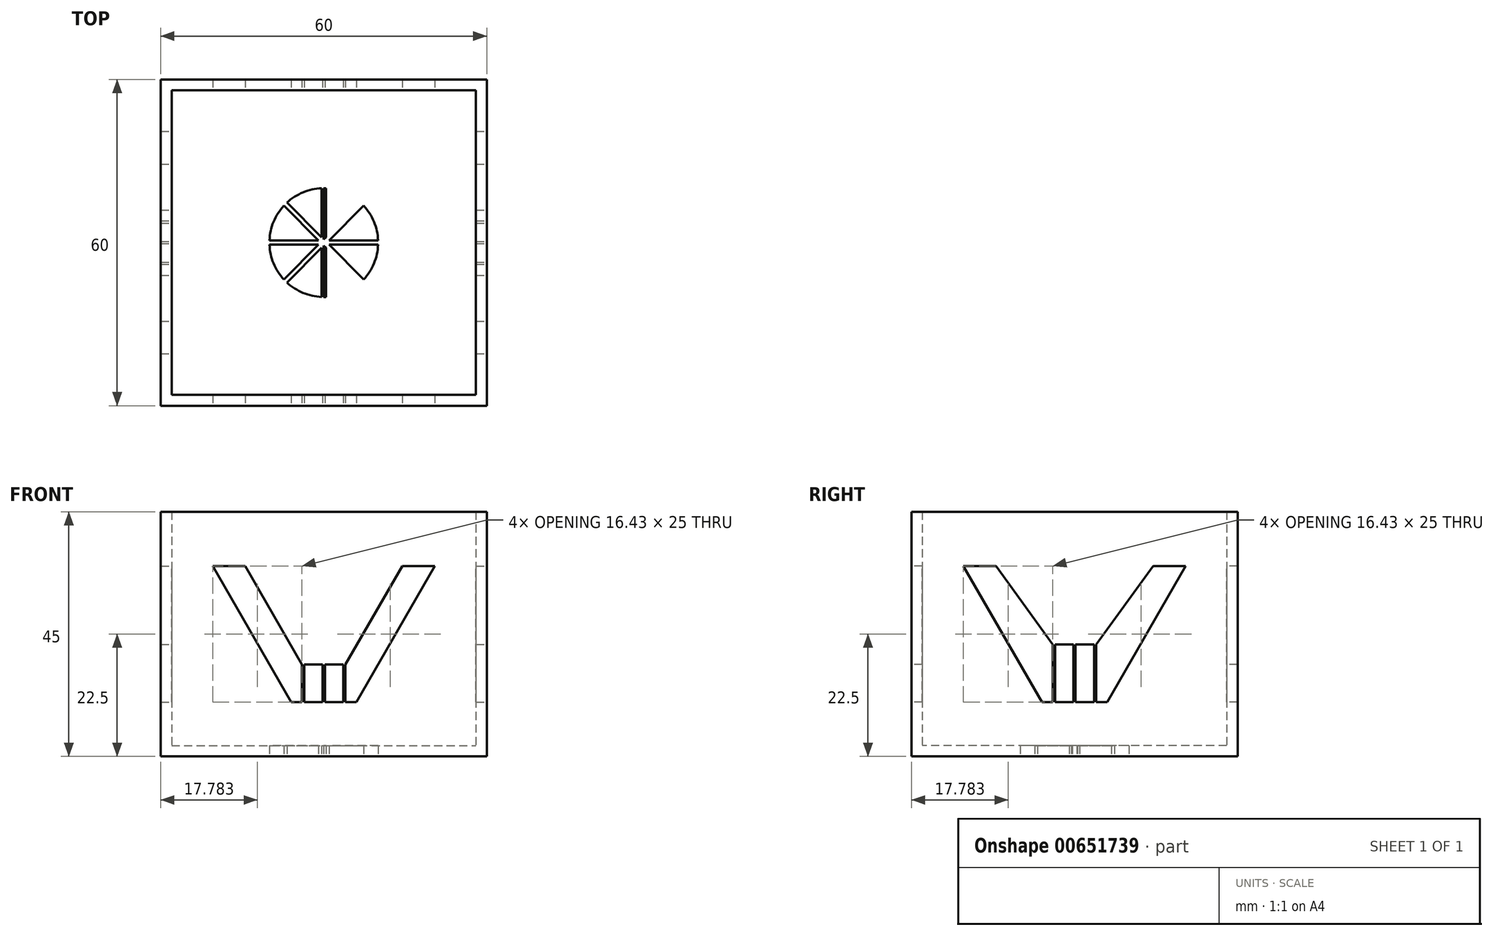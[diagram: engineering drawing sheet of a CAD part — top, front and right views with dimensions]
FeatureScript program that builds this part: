
annotation { "Feature Type Name" : "Feature", "Feature Type Description" : "" }
export const myFeature = defineFeature(function(context is Context, id is Id, definition is map)
    precondition{}
    {
        {
            var Q0;
            Q0=qCreatedBy(makeId("Top.planeOp"),FACE);
            var sketch = newSketch(context, id + "F0", { "sketchPlane" : qUnion([Q0])});
            skLineSegment(sketch, "E0.bottom", {"start": v(-30, 30) * mm, "end": v(30, 30) * mm});
            skLineSegment(sketch, "E0.top", {"start": v(-30, -30) * mm, "end": v(30, -30) * mm});
            skLineSegment(sketch, "E0.left", {"start": v(-30, 30) * mm, "end": v(-30, -30) * mm});
            skLineSegment(sketch, "E0.right", {"start": v(30, 30) * mm, "end": v(30, -30) * mm});
            skSolve(sketch);
        }
        {
            var Q0;
            Q0=makeQuery(id+"F0.imprint","IMPRINT",FACE,{"disambiguationData":[TD([[makeQuery(id+"F0.imprint","IMPRINT",EDGE,{"derivedFrom":sQuery(id+"F0.wireOp",EDGE,"E0.bottom")}),-1.0]])]});
            var Q1;
            Q1 = qSketchRegion(id + "F3", true);
            extrude(context, id + "F1", {"entities" : qUnion([Q0, Q1]), "depth" : 45 * mm, "offsetDistance" : 25 * mm});
        }
        {
            var Q0;
            Q0=makeQuery(id+"F1.opExtrude","CAP_FACE",FACE,{"disambiguationData":[OSD([sQuery(id+"F0.wireOp",EDGE,"E0.bottom"),sQuery(id+"F0.wireOp",EDGE,"E0.top"),sQuery(id+"F0.wireOp",EDGE,"E0.left"),sQuery(id+"F0.wireOp",EDGE,"E0.right")])],"isStart":false});
            shell(context, id + "F2", {"entities" : qUnion([Q0]), "thickness" : 2 * mm});
        }
        {
            var Q0;
            Q0=makeQuery(id+"F1.opExtrude","SWEPT_FACE",FACE,{"disambiguationData":[OSD([sQuery(id+"F0.wireOp",EDGE,"E0.top")])]});
            var sketch = newSketch(context, id + "F3", { "sketchPlane" : qUnion([Q0])});
            skLineSegment(sketch, "E1", {"start": v(-6, 10) * mm, "end": v(6, 10) * mm});
            skLineSegment(sketch, "E2", {"start": v(6, 10) * mm, "end": v(20.43, 35) * mm});
            skLineSegment(sketch, "E3", {"start": v(-6, 10) * mm, "end": v(-20.43, 35) * mm});
            skLineSegment(sketch, "E4", {"start": v(20.43, 35) * mm, "end": v(20.43, 45) * mm});
            skLineSegment(sketch, "E5", {"start": v(-20.43, 35) * mm, "end": v(-14.43, 35) * mm});
            skLineSegment(sketch, "E6", {"start": v(20.43, 35) * mm, "end": v(14.43, 35) * mm});
            skLineSegment(sketch, "E7", {"start": v(-14.43, 35) * mm, "end": v(-4, 16.93) * mm});
            skLineSegment(sketch, "E8", {"start": v(14.43, 35) * mm, "end": v(4, 16.93) * mm});
            skLineSegment(sketch, "E9", {"start": v(-4, 16.93) * mm, "end": v(4, 16.93) * mm});
            skLineSegment(sketch, "E10", {"start": v(-4, 16.93) * mm, "end": v(-4, 10) * mm});
            skLineSegment(sketch, "E11", {"start": v(-3.6, 16.93) * mm, "end": v(-3.6, 10) * mm});
            skLineSegment(sketch, "E12", {"start": v(4, 16.93) * mm, "end": v(4, 10) * mm});
            skLineSegment(sketch, "E13", {"start": v(3.6, 16.93) * mm, "end": v(3.6, 10) * mm});
            skLineSegment(sketch, "E14", {"start": v(0, 16.93) * mm, "end": v(0, 10) * mm});
            skLineSegment(sketch, "E15", {"start": v(0.2, 16.93) * mm, "end": v(0.2, 10) * mm});
            skLineSegment(sketch, "E16", {"start": v(-0.2, 16.93) * mm, "end": v(-0.2, 10) * mm});
            skSolve(sketch);
        }
        {
            var Q0;
            {var subQ0=sQuery(id+"F3.wireOp",EDGE,"E3");Q0=makeQuery(id+"F3.imprint","IMPRINT",FACE,{"disambiguationData":[TD([[makeQuery(id+"F3.imprint","IMPRINT",EDGE,{"derivedFrom":subQ0}),-1.0]])]});}
            var Q1;
            {var subQ0=sQuery(id+"F3.wireOp",EDGE,"E11");Q1=makeQuery(id+"F3.imprint","IMPRINT",FACE,{"disambiguationData":[TD([[makeQuery(id+"F3.imprint","IMPRINT",EDGE,{"derivedFrom":subQ0}),1.0]])]});}
            var Q2;
            {var subQ0=sQuery(id+"F3.wireOp",EDGE,"E13");Q2=makeQuery(id+"F3.imprint","IMPRINT",FACE,{"disambiguationData":[TD([[makeQuery(id+"F3.imprint","IMPRINT",EDGE,{"derivedFrom":subQ0}),-1.0]])]});}
            var Q3;
            {var subQ1=sQuery(id+"F3.wireOp",EDGE,"E2");Q3=makeQuery(id+"F3.imprint","IMPRINT",FACE,{"disambiguationData":[TD([[makeQuery(id+"F3.imprint","IMPRINT",EDGE,{"derivedFrom":subQ1}),1.0]])]});}
            extrude(context, id + "F4", {"entities" : qUnion([Q0, Q1, Q2, Q3]), "operationType" : NewBodyOperationType.REMOVE, "oppositeDirection" : true, "depth" : 64.2 * mm, "offsetDistance" : 25 * mm});
        }
        {
            var Q0;
            Q0=makeQuery(id+"F1.opExtrude","SWEPT_FACE",FACE,{"disambiguationData":[OSD([sQuery(id+"F0.wireOp",EDGE,"E0.right")])]});
            var sketch = newSketch(context, id + "F5", { "sketchPlane" : qUnion([Q0])});
            skLineSegment(sketch, "E17", {"start": v(-6, 10) * mm, "end": v(6, 10) * mm});
            skLineSegment(sketch, "E18", {"start": v(6, 10) * mm, "end": v(20.43, 35) * mm});
            skLineSegment(sketch, "E19", {"start": v(-6, 10) * mm, "end": v(-20.43, 35) * mm});
            skLineSegment(sketch, "E20", {"start": v(-20.43, 35) * mm, "end": v(-14.43, 35) * mm});
            skLineSegment(sketch, "E21", {"start": v(20.43, 35) * mm, "end": v(14.43, 35) * mm});
            skLineSegment(sketch, "E22", {"start": v(-14.43, 35) * mm, "end": v(-4, 20.58) * mm});
            skLineSegment(sketch, "E23", {"start": v(14.43, 35) * mm, "end": v(4, 20.58) * mm});
            skLineSegment(sketch, "E24", {"start": v(-4, 20.58) * mm, "end": v(4, 20.58) * mm});
            skLineSegment(sketch, "E25", {"start": v(-4, 20.58) * mm, "end": v(-4, 10) * mm});
            skLineSegment(sketch, "E26", {"start": v(-3.6, 20.58) * mm, "end": v(-3.6, 10) * mm});
            skLineSegment(sketch, "E27", {"start": v(4, 20.58) * mm, "end": v(4, 10) * mm});
            skLineSegment(sketch, "E28", {"start": v(3.6, 20.58) * mm, "end": v(3.6, 10) * mm});
            skLineSegment(sketch, "E29", {"start": v(0, 20.58) * mm, "end": v(0, 10) * mm});
            skLineSegment(sketch, "E30", {"start": v(0.2, 20.58) * mm, "end": v(0.2, 10) * mm});
            skLineSegment(sketch, "E31", {"start": v(-0.2, 20.58) * mm, "end": v(-0.2, 10) * mm});
            skSolve(sketch);
        }
        {
            var Q0;
            {var subQ0=sQuery(id+"F5.wireOp",EDGE,"E19");Q0=makeQuery(id+"F5.imprint","IMPRINT",FACE,{"disambiguationData":[TD([[makeQuery(id+"F5.imprint","IMPRINT",EDGE,{"derivedFrom":subQ0}),-1.0]])]});}
            var Q1;
            {var subQ0=sQuery(id+"F5.wireOp",EDGE,"E26");Q1=makeQuery(id+"F5.imprint","IMPRINT",FACE,{"disambiguationData":[TD([[makeQuery(id+"F5.imprint","IMPRINT",EDGE,{"derivedFrom":subQ0}),1.0]])]});}
            var Q2;
            {var subQ0=sQuery(id+"F5.wireOp",EDGE,"E28");Q2=makeQuery(id+"F5.imprint","IMPRINT",FACE,{"disambiguationData":[TD([[makeQuery(id+"F5.imprint","IMPRINT",EDGE,{"derivedFrom":subQ0}),-1.0]])]});}
            var Q3;
            {var subQ1=sQuery(id+"F5.wireOp",EDGE,"E18");Q3=makeQuery(id+"F5.imprint","IMPRINT",FACE,{"disambiguationData":[TD([[makeQuery(id+"F5.imprint","IMPRINT",EDGE,{"derivedFrom":subQ1}),1.0]])]});}
            extrude(context, id + "F6", {"entities" : qUnion([Q0, Q1, Q2, Q3]), "operationType" : NewBodyOperationType.REMOVE, "oppositeDirection" : true, "depth" : 63.5 * mm, "offsetDistance" : 25 * mm});
        }
        {
            var Q0;
            Q0=makeQuery(id+"F1.opExtrude","CAP_FACE",FACE,{"disambiguationData":[OSD([sQuery(id+"F0.wireOp",EDGE,"E0.bottom"),sQuery(id+"F0.wireOp",EDGE,"E0.top"),sQuery(id+"F0.wireOp",EDGE,"E0.left"),sQuery(id+"F0.wireOp",EDGE,"E0.right")])],"isStart":true});
            var sketch = newSketch(context, id + "F7", { "sketchPlane" : qUnion([Q0])});
            skCircle(sketch, "E32", {"center": v(0, 0) * mm, "radius": 10 * mm});
            skLineSegment(sketch, "E33", {"start": v(0, 10) * mm, "end": v(0, -10) * mm});
            skLineSegment(sketch, "E34", {"start": v(-10, 0) * mm, "end": v(10, 0) * mm});
            skLineSegment(sketch, "E35", {"start": v(-10, -0.4) * mm, "end": v(10, -0.4) * mm});
            skLineSegment(sketch, "E36", {"start": v(-10, 0.4) * mm, "end": v(10, 0.4) * mm});
            skLineSegment(sketch, "E37", {"start": v(0.4, 10) * mm, "end": v(0.4, -10) * mm});
            skLineSegment(sketch, "E38", {"start": v(-0.4, 10) * mm, "end": v(-0.4, -10) * mm});
            skLineSegment(sketch, "E39", {"start": v(-7.07, -7.07) * mm, "end": v(7.07, 7.07) * mm});
            skLineSegment(sketch, "E40", {"start": v(7.07, -7.07) * mm, "end": v(-7.07, 7.07) * mm});
            skLineSegment(sketch, "E41", {"start": v(-6.78, -7.35) * mm, "end": v(7.35, 6.78) * mm});
            skLineSegment(sketch, "E42", {"start": v(-7.35, -6.78) * mm, "end": v(6.78, 7.35) * mm});
            skLineSegment(sketch, "E43", {"start": v(6.78, -7.35) * mm, "end": v(-7.35, 6.78) * mm});
            skLineSegment(sketch, "E44", {"start": v(7.35, -6.78) * mm, "end": v(-6.78, 7.35) * mm});
            skSolve(sketch);
        }
        {
            var Q0;
            {var subQ0=sQuery(id+"F7.wireOp",EDGE,"E38");var subQ1=sQuery(id+"F7.wireOp",EDGE,"E32");var subQ2=makeQuery(id+"F7.imprint","INTERSECT",VERTEX,{"disambiguationData":[OD(0.0)],"derivedFrom":[subQ1,subQ0]});Q0=makeQuery(id+"F7.imprint","IMPRINT",FACE,{"disambiguationData":[TD([[makeQuery(id+"F7.imprint","IMPRINT",EDGE,{"disambiguationData":[TD([[subQ2,-1.0]])],"derivedFrom":subQ1}),1.0]])]});}
            var Q1;
            {var subQ0=sQuery(id+"F7.wireOp",EDGE,"E37");var subQ1=sQuery(id+"F7.wireOp",EDGE,"E32");var subQ2=makeQuery(id+"F7.imprint","INTERSECT",VERTEX,{"disambiguationData":[OD(0.0)],"derivedFrom":[subQ1,subQ0]});Q1=makeQuery(id+"F7.imprint","IMPRINT",FACE,{"disambiguationData":[TD([[makeQuery(id+"F7.imprint","IMPRINT",EDGE,{"disambiguationData":[TD([[subQ2,1.0]])],"derivedFrom":subQ1}),1.0]])]});}
            var Q2;
            {var subQ0=sQuery(id+"F7.wireOp",EDGE,"E36");var subQ1=sQuery(id+"F7.wireOp",EDGE,"E32");var subQ2=makeQuery(id+"F7.imprint","INTERSECT",VERTEX,{"disambiguationData":[OD(1.0)],"derivedFrom":[subQ1,subQ0]});Q2=makeQuery(id+"F7.imprint","IMPRINT",FACE,{"disambiguationData":[TD([[makeQuery(id+"F7.imprint","IMPRINT",EDGE,{"disambiguationData":[TD([[subQ2,-1.0]])],"derivedFrom":subQ1}),1.0]])]});}
            var Q3;
            {var subQ0=sQuery(id+"F7.wireOp",EDGE,"E35");var subQ1=sQuery(id+"F7.wireOp",EDGE,"E32");var subQ2=makeQuery(id+"F7.imprint","INTERSECT",VERTEX,{"disambiguationData":[OD(1.0)],"derivedFrom":[subQ1,subQ0]});Q3=makeQuery(id+"F7.imprint","IMPRINT",FACE,{"disambiguationData":[TD([[makeQuery(id+"F7.imprint","IMPRINT",EDGE,{"disambiguationData":[TD([[subQ2,1.0]])],"derivedFrom":subQ1}),1.0]])]});}
            var Q4;
            {var subQ0=sQuery(id+"F7.wireOp",EDGE,"E37");var subQ1=sQuery(id+"F7.wireOp",EDGE,"E32");var subQ2=makeQuery(id+"F7.imprint","INTERSECT",VERTEX,{"disambiguationData":[OD(1.0)],"derivedFrom":[subQ1,subQ0]});Q4=makeQuery(id+"F7.imprint","IMPRINT",FACE,{"disambiguationData":[TD([[makeQuery(id+"F7.imprint","IMPRINT",EDGE,{"disambiguationData":[TD([[subQ2,-1.0]])],"derivedFrom":subQ1}),1.0]])]});}
            var Q5;
            {var subQ0=sQuery(id+"F7.wireOp",EDGE,"E38");var subQ1=sQuery(id+"F7.wireOp",EDGE,"E32");var subQ2=makeQuery(id+"F7.imprint","INTERSECT",VERTEX,{"disambiguationData":[OD(1.0)],"derivedFrom":[subQ1,subQ0]});Q5=makeQuery(id+"F7.imprint","IMPRINT",FACE,{"disambiguationData":[TD([[makeQuery(id+"F7.imprint","IMPRINT",EDGE,{"disambiguationData":[TD([[subQ2,1.0]])],"derivedFrom":subQ1}),1.0]])]});}
            var Q6;
            {var subQ0=sQuery(id+"F7.wireOp",EDGE,"E35");var subQ1=sQuery(id+"F7.wireOp",EDGE,"E32");var subQ2=makeQuery(id+"F7.imprint","INTERSECT",VERTEX,{"disambiguationData":[OD(0.0)],"derivedFrom":[subQ1,subQ0]});Q6=makeQuery(id+"F7.imprint","IMPRINT",FACE,{"disambiguationData":[TD([[makeQuery(id+"F7.imprint","IMPRINT",EDGE,{"disambiguationData":[TD([[subQ2,-1.0]])],"derivedFrom":subQ1}),1.0]])]});}
            var Q7;
            {var subQ0=sQuery(id+"F7.wireOp",EDGE,"E36");var subQ1=sQuery(id+"F7.wireOp",EDGE,"E32");var subQ2=makeQuery(id+"F7.imprint","INTERSECT",VERTEX,{"disambiguationData":[OD(0.0)],"derivedFrom":[subQ1,subQ0]});Q7=makeQuery(id+"F7.imprint","IMPRINT",FACE,{"disambiguationData":[TD([[makeQuery(id+"F7.imprint","IMPRINT",EDGE,{"disambiguationData":[TD([[subQ2,1.0]])],"derivedFrom":subQ1}),1.0]])]});}
            extrude(context, id + "F8", {"entities" : qUnion([Q0, Q1, Q2, Q3, Q4, Q5, Q6, Q7]), "operationType" : NewBodyOperationType.REMOVE, "oppositeDirection" : true, "depth" : 25 * mm, "offsetDistance" : 25 * mm});
        }
    });
